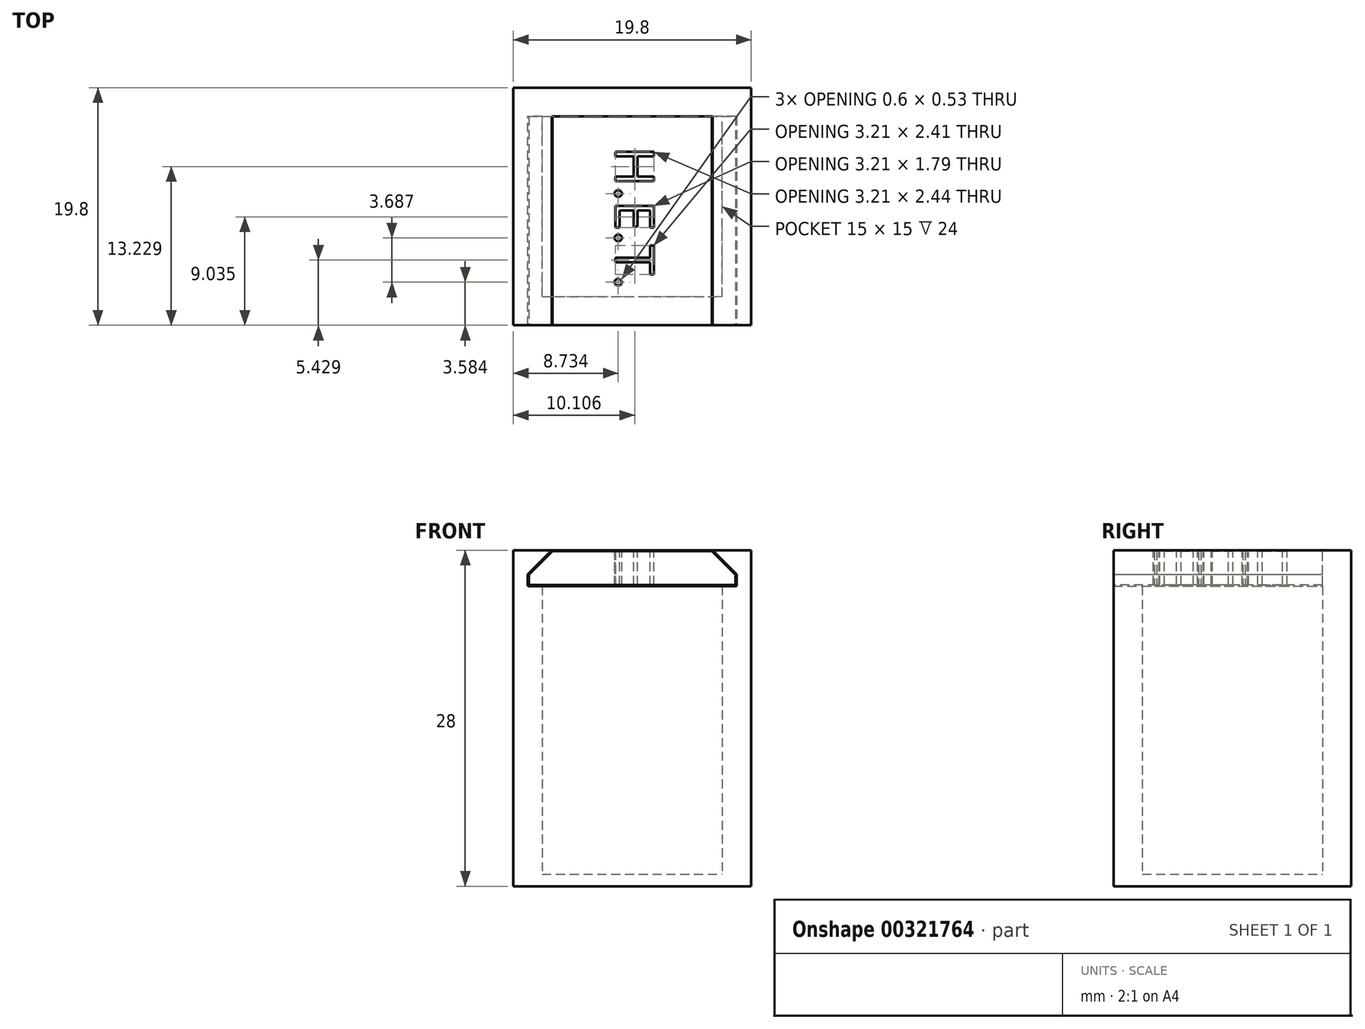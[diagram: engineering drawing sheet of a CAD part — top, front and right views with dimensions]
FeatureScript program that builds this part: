
annotation { "Feature Type Name" : "Feature", "Feature Type Description" : "" }
export const myFeature = defineFeature(function(context is Context, id is Id, definition is map)
    precondition{}
    {
        {
            var Q0;
            Q0=qCreatedBy(makeId("Top.planeOp"),FACE);
            var sketch = newSketch(context, id + "F0", { "sketchPlane" : qUnion([Q0])});
            skLineSegment(sketch, "E0.bottom", {"start": v(-7.5, -7.5) * mm, "end": v(7.5, -7.5) * mm});
            skLineSegment(sketch, "E0.top", {"start": v(-7.5, 7.5) * mm, "end": v(7.5, 7.5) * mm});
            skLineSegment(sketch, "E0.left", {"start": v(-7.5, -7.5) * mm, "end": v(-7.5, 7.5) * mm});
            skLineSegment(sketch, "E0.right", {"start": v(7.5, -7.5) * mm, "end": v(7.5, 7.5) * mm});
            skLineSegment(sketch, "E1", {"start": v(-7.5, 7.5) * mm, "end": v(-7.5, 9.9) * mm});
            skLineSegment(sketch, "E2", {"start": v(-7.5, 9.9) * mm, "end": v(-9.9, 9.9) * mm});
            skLineSegment(sketch, "E3", {"start": v(7.5, -7.5) * mm, "end": v(9.9, -7.5) * mm});
            skLineSegment(sketch, "E4", {"start": v(9.9, -7.5) * mm, "end": v(9.9, -9.9) * mm});
            skLineSegment(sketch, "E5", {"start": v(-7.5, 0) * mm, "end": v(0, 0) * mm});
            skLineSegment(sketch, "E6", {"start": v(0, 0) * mm, "end": v(0, -7.5) * mm});
            skLineSegment(sketch, "E7.bottom", {"start": v(-9.9, 9.9) * mm, "end": v(9.9, 9.9) * mm});
            skLineSegment(sketch, "E7.top", {"start": v(-9.9, -9.9) * mm, "end": v(9.9, -9.9) * mm});
            skLineSegment(sketch, "E7.left", {"start": v(-9.9, 9.9) * mm, "end": v(-9.9, -9.9) * mm});
            skLineSegment(sketch, "E7.right", {"start": v(9.9, 9.9) * mm, "end": v(9.9, -9.9) * mm});
            skSolve(sketch);
        }
        {
            var Q0;
            {var subQ0=sQuery(id+"F0.wireOp",EDGE,"E1");Q0=makeQuery(id+"F0.imprint","IMPRINT",FACE,{"disambiguationData":[TD([[makeQuery(id+"F0.imprint","IMPRINT",EDGE,{"derivedFrom":subQ0}),1.0]])]});}
            var Q1;
            Q1=makeQuery(id+"F0.imprint","IMPRINT",FACE,{"disambiguationData":[TD([[makeQuery(id+"F0.imprint","IMPRINT",EDGE,{"derivedFrom":sQuery(id+"F0.wireOp",EDGE,"E0.top")}),1.0]])]});
            extrude(context, id + "F1", {"entities" : qUnion([Q0, Q1]), "depth" : 25 * mm});
        }
        {
            var Q0;
            Q0=makeQuery(id+"F1.opExtrude","CAP_FACE",FACE,{"disambiguationData":[OSD([sQuery(id+"F0.wireOp",EDGE,"E0.bottom"),sQuery(id+"F0.wireOp",EDGE,"E0.top"),sQuery(id+"F0.wireOp",EDGE,"E0.left"),sQuery(id+"F0.wireOp",EDGE,"E0.right"),sQuery(id+"F0.wireOp",EDGE,"E7.bottom"),sQuery(id+"F0.wireOp",EDGE,"E7.top"),sQuery(id+"F0.wireOp",EDGE,"E7.left"),sQuery(id+"F0.wireOp",EDGE,"E7.right")])],"isStart":true});
            var sketch = newSketch(context, id + "F2", { "sketchPlane" : qUnion([Q0])});
            skLineSegment(sketch, "E8.bottom", {"start": v(-9.9, 9.9) * mm, "end": v(9.9, 9.9) * mm});
            skLineSegment(sketch, "E8.top", {"start": v(-9.9, -9.9) * mm, "end": v(9.9, -9.9) * mm});
            skLineSegment(sketch, "E8.left", {"start": v(-9.9, 9.9) * mm, "end": v(-9.9, -9.9) * mm});
            skLineSegment(sketch, "E8.right", {"start": v(9.9, 9.9) * mm, "end": v(9.9, -9.9) * mm});
            skSolve(sketch);
        }
        {
            var Q0;
            Q0=qSketchRegion(id+"F2",true);
            extrude(context, id + "F3", {"entities" : qUnion([Q0]), "operationType" : NewBodyOperationType.ADD, "depth" : 1 * mm});
        }
        {
            var Q0;
            Q0=makeQuery(id+"F1.opExtrude","CAP_FACE",FACE,{"disambiguationData":[OSD([sQuery(id+"F0.wireOp",EDGE,"E0.bottom"),sQuery(id+"F0.wireOp",EDGE,"E0.top"),sQuery(id+"F0.wireOp",EDGE,"E0.left"),sQuery(id+"F0.wireOp",EDGE,"E0.right"),sQuery(id+"F0.wireOp",EDGE,"E7.bottom"),sQuery(id+"F0.wireOp",EDGE,"E7.top"),sQuery(id+"F0.wireOp",EDGE,"E7.left"),sQuery(id+"F0.wireOp",EDGE,"E7.right")])],"isStart":false});
            var sketch = newSketch(context, id + "F4", { "sketchPlane" : qUnion([Q0])});
            skLineSegment(sketch, "E9", {"start": v(-9.9, 0) * mm, "end": v(-8.7, 0) * mm});
            skPoint(sketch, "E9.endSnap0", {"position": v(-7.5, 0) * mm});
            skLineSegment(sketch, "E10", {"start": v(9.9, 0) * mm, "end": v(8.7, 0) * mm});
            skLineSegment(sketch, "E11", {"start": v(-8.7, 0) * mm, "end": v(-8.7, -10.6) * mm});
            skLineSegment(sketch, "E12", {"start": v(8.7, 0) * mm, "end": v(8.7, -11.22) * mm});
            skLineSegment(sketch, "E13", {"start": v(-8.7, -10.6) * mm, "end": v(8.7, -10.6) * mm});
            skLineSegment(sketch, "E14", {"start": v(-7.5, 7.5) * mm, "end": v(-9.9, 7.5) * mm});
            skLineSegment(sketch, "E15", {"start": v(7.5, 7.5) * mm, "end": v(9.9, 7.5) * mm});
            skLineSegment(sketch, "E16", {"start": v(-8.7, 0) * mm, "end": v(-8.7, 7.5) * mm});
            skLineSegment(sketch, "E17", {"start": v(8.7, 0) * mm, "end": v(8.7, 7.5) * mm});
            skLineSegment(sketch, "E18", {"start": v(-7.5, 7.5) * mm, "end": v(7.5, 7.5) * mm});
            skSolve(sketch);
        }
        {
            var Q0;
            {var subQ11=sQuery(id+"F4.wireOp",EDGE,"E16");Q0=makeQuery(id+"F4.imprint","IMPRINT",FACE,{"disambiguationData":[TD([[makeQuery(id+"F4.imprint","IMPRINT",EDGE,{"derivedFrom":subQ11}),-1.0]])]});}
            extrude(context, id + "F5", {"entities" : qUnion([Q0]), "operationType" : NewBodyOperationType.REMOVE, "oppositeDirection" : true, "depth" : 2 * mm});
        }
        {
            var Q0;
            Q0=makeQuery(id+"F3.boolean.opBoolean","MERGE",FACE,{"derivedFrom":[makeQuery(id+"F1.opExtrude","SWEPT_FACE",FACE,{"disambiguationData":[OSD([sQuery(id+"F0.wireOp",EDGE,"E7.top")])]}),makeQuery(id+"F3.opExtrude","SWEPT_FACE",FACE,{"disambiguationData":[OSD([sQuery(id+"F2.wireOp",EDGE,"E8.bottom")])]})]});
            var sketch = newSketch(context, id + "F6", { "sketchPlane" : qUnion([Q0])});
            skLineSegment(sketch, "E19", {"start": v(-9.9, 25) * mm, "end": v(-9.9, 27) * mm});
            skLineSegment(sketch, "E20", {"start": v(9.9, 25) * mm, "end": v(9.9, 27) * mm});
            skLineSegment(sketch, "E21", {"start": v(-9.9, 27) * mm, "end": v(9.9, 27) * mm});
            skLineSegment(sketch, "E22", {"start": v(-8.7, 25) * mm, "end": v(-6.7, 27) * mm});
            skLineSegment(sketch, "E23", {"start": v(8.7, 25) * mm, "end": v(6.7, 27) * mm});
            skLineSegment(sketch, "E24", {"start": v(-9.9, 25) * mm, "end": v(-8.7, 25) * mm});
            skLineSegment(sketch, "E25", {"start": v(8.7, 25) * mm, "end": v(9.9, 25) * mm});
            skSolve(sketch);
        }
        {
            var Q0;
            Q0=makeQuery(id+"F5.boolean.opBoolean","COPY",FACE,{"derivedFrom":makeQuery(id+"F5.opExtrude","CAP_FACE",FACE,{"disambiguationData":[OSD([sQuery(id+"F0.wireOp",EDGE,"E0.bottom"),sQuery(id+"F0.wireOp",EDGE,"E0.left"),sQuery(id+"F0.wireOp",EDGE,"E0.right"),sQuery(id+"F0.wireOp",EDGE,"E7.top"),sQuery(id+"F4.wireOp",EDGE,"E11"),sQuery(id+"F4.wireOp",EDGE,"E12"),sQuery(id+"F4.wireOp",EDGE,"E14"),sQuery(id+"F4.wireOp",EDGE,"E15"),sQuery(id+"F4.wireOp",EDGE,"E16"),sQuery(id+"F4.wireOp",EDGE,"E17")])],"isStart":false})});
            extrude(context, id + "F7", {"entities" : qUnion([Q0]), "operationType" : NewBodyOperationType.ADD, "depth" : 1 * mm});
        }
        {
            var Q0;
            {var subQ0=sQuery(id+"F6.wireOp",EDGE,"E19");Q0=makeQuery(id+"F6.imprint","IMPRINT",FACE,{"disambiguationData":[TD([[makeQuery(id+"F6.imprint","IMPRINT",EDGE,{"derivedFrom":subQ0}),-1.0]])]});}
            var Q1;
            {var subQ0=sQuery(id+"F6.wireOp",EDGE,"E20");Q1=makeQuery(id+"F6.imprint","IMPRINT",FACE,{"disambiguationData":[TD([[makeQuery(id+"F6.imprint","IMPRINT",EDGE,{"derivedFrom":subQ0}),1.0]])]});}
            var Q2;
            Q2=makeQuery(id+"F3.boolean.opBoolean","MERGE",FACE,{"derivedFrom":[makeQuery(id+"F1.opExtrude","SWEPT_FACE",FACE,{"disambiguationData":[OSD([sQuery(id+"F0.wireOp",EDGE,"E7.bottom")])]}),makeQuery(id+"F3.opExtrude","SWEPT_FACE",FACE,{"disambiguationData":[OSD([sQuery(id+"F2.wireOp",EDGE,"E8.top")])]})]});
            extrude(context, id + "F8", {"entities" : qUnion([Q0, Q1]), "operationType" : NewBodyOperationType.ADD, "endBound" : BoundingType.UP_TO_SURFACE, "oppositeDirection" : true, "endBoundEntityFace" : qUnion([Q2]), "depth" : 25 * mm});
        }
        {
            var Q0;
            {var subQ0=sQuery(id+"F6.wireOp",EDGE,"E21");var subQ1=sQuery(id+"F2.wireOp",EDGE,"E8.top");var subQ2=sQuery(id+"F0.wireOp",EDGE,"E7.bottom");Q0=makeQuery(id+"F8.boolean.opBoolean","MERGE",FACE,{"derivedFrom":[makeQuery(id+"F3.boolean.opBoolean","MERGE",FACE,{"derivedFrom":[makeQuery(id+"F1.opExtrude","SWEPT_FACE",FACE,{"disambiguationData":[OSD([subQ2])]}),makeQuery(id+"F3.opExtrude","SWEPT_FACE",FACE,{"disambiguationData":[OSD([subQ1])]})]}),makeQuery(id+"F8.opExtrude","CAP_FACE",FACE,{"disambiguationData":[OSD([subQ2,subQ1]),ownerDisambiguation([makeQuery(id+"F8.opExtrude","SWEPT_BODY",BODY,{"disambiguationData":[OSD([sQuery(id+"F6.wireOp",EDGE,"E19"),subQ0,sQuery(id+"F6.wireOp",EDGE,"E22"),sQuery(id+"F6.wireOp",EDGE,"E24")])]})])],"isStart":false}),makeQuery(id+"F8.opExtrude","CAP_FACE",FACE,{"disambiguationData":[OSD([subQ2,subQ1]),ownerDisambiguation([makeQuery(id+"F8.opExtrude","SWEPT_BODY",BODY,{"disambiguationData":[OSD([sQuery(id+"F6.wireOp",EDGE,"E20"),subQ0,sQuery(id+"F6.wireOp",EDGE,"E23"),sQuery(id+"F6.wireOp",EDGE,"E25")])]})])],"isStart":false})]});}
            var sketch = newSketch(context, id + "F9", { "sketchPlane" : qUnion([Q0])});
            skLineSegment(sketch, "E26", {"start": v(-6.7, 27) * mm, "end": v(-6.7, 25) * mm});
            skLineSegment(sketch, "E27", {"start": v(-6.7, 25) * mm, "end": v(-8.7, 25) * mm});
            skLineSegment(sketch, "E28", {"start": v(-8.7, 25) * mm, "end": v(-6.7, 27) * mm});
            skLineSegment(sketch, "E29", {"start": v(6.7, 27) * mm, "end": v(6.7, 25) * mm});
            skLineSegment(sketch, "E30", {"start": v(6.7, 25) * mm, "end": v(8.7, 25) * mm});
            skLineSegment(sketch, "E31", {"start": v(8.7, 25) * mm, "end": v(6.7, 27) * mm});
            skSolve(sketch);
        }
        {
            var Q0;
            Q0=makeQuery(id+"F9.imprint","IMPRINT",FACE,{"disambiguationData":[TD([[makeQuery(id+"F9.imprint","IMPRINT",EDGE,{"derivedFrom":sQuery(id+"F9.wireOp",EDGE,"E26")}),-1.0]])]});
            var Q1;
            Q1=makeQuery(id+"F9.imprint","IMPRINT",FACE,{"disambiguationData":[TD([[makeQuery(id+"F9.imprint","IMPRINT",EDGE,{"derivedFrom":sQuery(id+"F9.wireOp",EDGE,"E29")}),1.0]])]});
            var Q2;
            Q2=makeQuery(id+"F5.boolean.opBoolean","MERGE",FACE,{"derivedFrom":[makeQuery(id+"F1.opExtrude","SWEPT_FACE",FACE,{"disambiguationData":[OSD([sQuery(id+"F0.wireOp",EDGE,"E0.top")])]}),makeQuery(id+"F5.opExtrude","SWEPT_FACE",FACE,{"disambiguationData":[OSD([sQuery(id+"F4.wireOp",EDGE,"E14")])]}),makeQuery(id+"F5.opExtrude","SWEPT_FACE",FACE,{"disambiguationData":[OSD([sQuery(id+"F4.wireOp",EDGE,"E15")])]})]});
            extrude(context, id + "F10", {"entities" : qUnion([Q0, Q1]), "operationType" : NewBodyOperationType.ADD, "endBound" : BoundingType.UP_TO_SURFACE, "oppositeDirection" : true, "endBoundEntityFace" : qUnion([Q2]), "depth" : 25 * mm});
        }
        {
            var Q0;
            Q0=makeQuery(id+"F1.opExtrude","CAP_FACE",FACE,{"disambiguationData":[OSD([sQuery(id+"F0.wireOp",EDGE,"E0.bottom"),sQuery(id+"F0.wireOp",EDGE,"E0.top"),sQuery(id+"F0.wireOp",EDGE,"E0.left"),sQuery(id+"F0.wireOp",EDGE,"E0.right"),sQuery(id+"F0.wireOp",EDGE,"E7.bottom"),sQuery(id+"F0.wireOp",EDGE,"E7.top"),sQuery(id+"F0.wireOp",EDGE,"E7.left"),sQuery(id+"F0.wireOp",EDGE,"E7.right")])],"isStart":false});
            var Q1;
            {var subQ0=sQuery(id+"F6.wireOp",EDGE,"E21");Q1=makeQuery(id+"F8.opExtrude","SWEPT_FACE",FACE,{"disambiguationData":[OSD([subQ0]),TDD([makeQuery(id+"F6.imprint","IMPRINT",EDGE,{"disambiguationData":[TD([[makeQuery(id+"F6.imprint","INTERSECT",VERTEX,{"derivedFrom":[sQuery(id+"F6.wireOp",EDGE,"E20"),subQ0]}),1.0]])],"derivedFrom":subQ0})])]});}
            extrude(context, id + "F11", {"entities" : qUnion([Q0]), "operationType" : NewBodyOperationType.ADD, "endBound" : BoundingType.UP_TO_SURFACE, "endBoundEntityFace" : qUnion([Q1]), "depth" : 25 * mm});
        }
        {
            var Q0;
            {var subQ0=sQuery(id+"F6.wireOp",EDGE,"E21");var subQ1=sQuery(id+"F0.wireOp",EDGE,"E7.top");Q0=makeQuery(id+"F8.boolean.opBoolean","MERGE",FACE,{"derivedFrom":[makeQuery(id+"F7.boolean.opBoolean","MERGE",FACE,{"derivedFrom":[makeQuery(id+"F3.boolean.opBoolean","MERGE",FACE,{"derivedFrom":[makeQuery(id+"F1.opExtrude","SWEPT_FACE",FACE,{"disambiguationData":[OSD([subQ1])]}),makeQuery(id+"F3.opExtrude","SWEPT_FACE",FACE,{"disambiguationData":[OSD([sQuery(id+"F2.wireOp",EDGE,"E8.bottom")])]})]}),makeQuery(id+"F7.opExtrude","SWEPT_FACE",FACE,{"disambiguationData":[OSD([subQ1])]})]}),makeQuery(id+"F8.opExtrude","CAP_FACE",FACE,{"disambiguationData":[OSD([sQuery(id+"F6.wireOp",EDGE,"E19"),subQ0,sQuery(id+"F6.wireOp",EDGE,"E22"),sQuery(id+"F6.wireOp",EDGE,"E24")])],"isStart":true}),makeQuery(id+"F8.opExtrude","CAP_FACE",FACE,{"disambiguationData":[OSD([sQuery(id+"F6.wireOp",EDGE,"E20"),subQ0,sQuery(id+"F6.wireOp",EDGE,"E23"),sQuery(id+"F6.wireOp",EDGE,"E25")])],"isStart":true})]});}
            var sketch = newSketch(context, id + "F12", { "sketchPlane" : qUnion([Q0])});
            skLineSegment(sketch, "E32.0", {"start": v(-8.6, 24.1) * mm, "end": v(-8.6, 24.96) * mm});
            skLineSegment(sketch, "E33.0", {"start": v(-8.6, 24.96) * mm, "end": v(-6.63, 26.93) * mm});
            skLineSegment(sketch, "E34.0", {"start": v(-8.6, 24.1) * mm, "end": v(8.6, 24.1) * mm});
            skLineSegment(sketch, "E35.0", {"start": v(8.6, 24.1) * mm, "end": v(8.6, 24.96) * mm});
            skLineSegment(sketch, "E36.0", {"start": v(8.6, 24.96) * mm, "end": v(6.63, 26.93) * mm});
            skLineSegment(sketch, "E37", {"start": v(-6.63, 26.93) * mm, "end": v(6.63, 26.93) * mm});
            skSolve(sketch);
        }
        {
            var Q0;
            Q0=makeQuery(id+"F12.imprint","IMPRINT",FACE,{"disambiguationData":[TD([[makeQuery(id+"F12.imprint","IMPRINT",EDGE,{"derivedFrom":sQuery(id+"F12.wireOp",EDGE,"E32.0")}),-1.0]])]});
            var Q1;
            {var subQ0=sQuery(id+"F4.wireOp",EDGE,"E15");var subQ1=sQuery(id+"F4.wireOp",EDGE,"E14");var subQ2=sQuery(id+"F0.wireOp",EDGE,"E0.top");Q1=makeQuery(id+"F11.boolean.opBoolean","MERGE",FACE,{"derivedFrom":[makeQuery(id+"F10.boolean.opBoolean","MERGE",FACE,{"derivedFrom":[makeQuery(id+"F5.boolean.opBoolean","MERGE",FACE,{"derivedFrom":[makeQuery(id+"F1.opExtrude","SWEPT_FACE",FACE,{"disambiguationData":[OSD([subQ2])]}),makeQuery(id+"F5.opExtrude","SWEPT_FACE",FACE,{"disambiguationData":[OSD([subQ1])]}),makeQuery(id+"F5.opExtrude","SWEPT_FACE",FACE,{"disambiguationData":[OSD([subQ0])]})]}),makeQuery(id+"F10.opExtrude","CAP_FACE",FACE,{"disambiguationData":[OSD([subQ2,subQ1,subQ0]),ownerDisambiguation([makeQuery(id+"F10.opExtrude","SWEPT_BODY",BODY,{"disambiguationData":[OSD([sQuery(id+"F9.wireOp",EDGE,"E26"),sQuery(id+"F9.wireOp",EDGE,"E27"),sQuery(id+"F9.wireOp",EDGE,"E28")])]})])],"isStart":false}),makeQuery(id+"F10.opExtrude","CAP_FACE",FACE,{"disambiguationData":[OSD([subQ2,subQ1,subQ0]),ownerDisambiguation([makeQuery(id+"F10.opExtrude","SWEPT_BODY",BODY,{"disambiguationData":[OSD([sQuery(id+"F9.wireOp",EDGE,"E29"),sQuery(id+"F9.wireOp",EDGE,"E30"),sQuery(id+"F9.wireOp",EDGE,"E31")])]})])],"isStart":false})]}),makeQuery(id+"F11.opExtrude","SWEPT_FACE",FACE,{"disambiguationData":[OSD([subQ2,subQ1,subQ0])]})]});}
            extrude(context, id + "F13", {"entities" : qUnion([Q0]), "endBound" : BoundingType.UP_TO_SURFACE, "oppositeDirection" : true, "endBoundEntityFace" : qUnion([Q1]), "depth" : 25 * mm});
        }
        {
            var Q0;
            Q0=makeQuery(id+"F13.opExtrude","SWEPT_FACE",FACE,{"disambiguationData":[OSD([sQuery(id+"F12.wireOp",EDGE,"E37")])]});
            var sketch = newSketch(context, id + "F14", { "sketchPlane" : qUnion([Q0])});
            skText(sketch, "E38", { "text": "H.E.T.", "fontName": "OpenSans-Regular.ttf"});
            const initialGuessF14  = {"E38": [-0.0014, 0.00499, 0, -1, 0.00324]};
            skSetInitialGuess(sketch, initialGuessF14);
            skSolve(sketch);
        }
        {
            var Q0;
            Q0=qSketchRegion(id+"F14",true);
            extrude(context, id + "F15", {"entities" : qUnion([Q0]), "operationType" : NewBodyOperationType.REMOVE, "oppositeDirection" : true, "depth" : 3 * mm});
        }
    });
